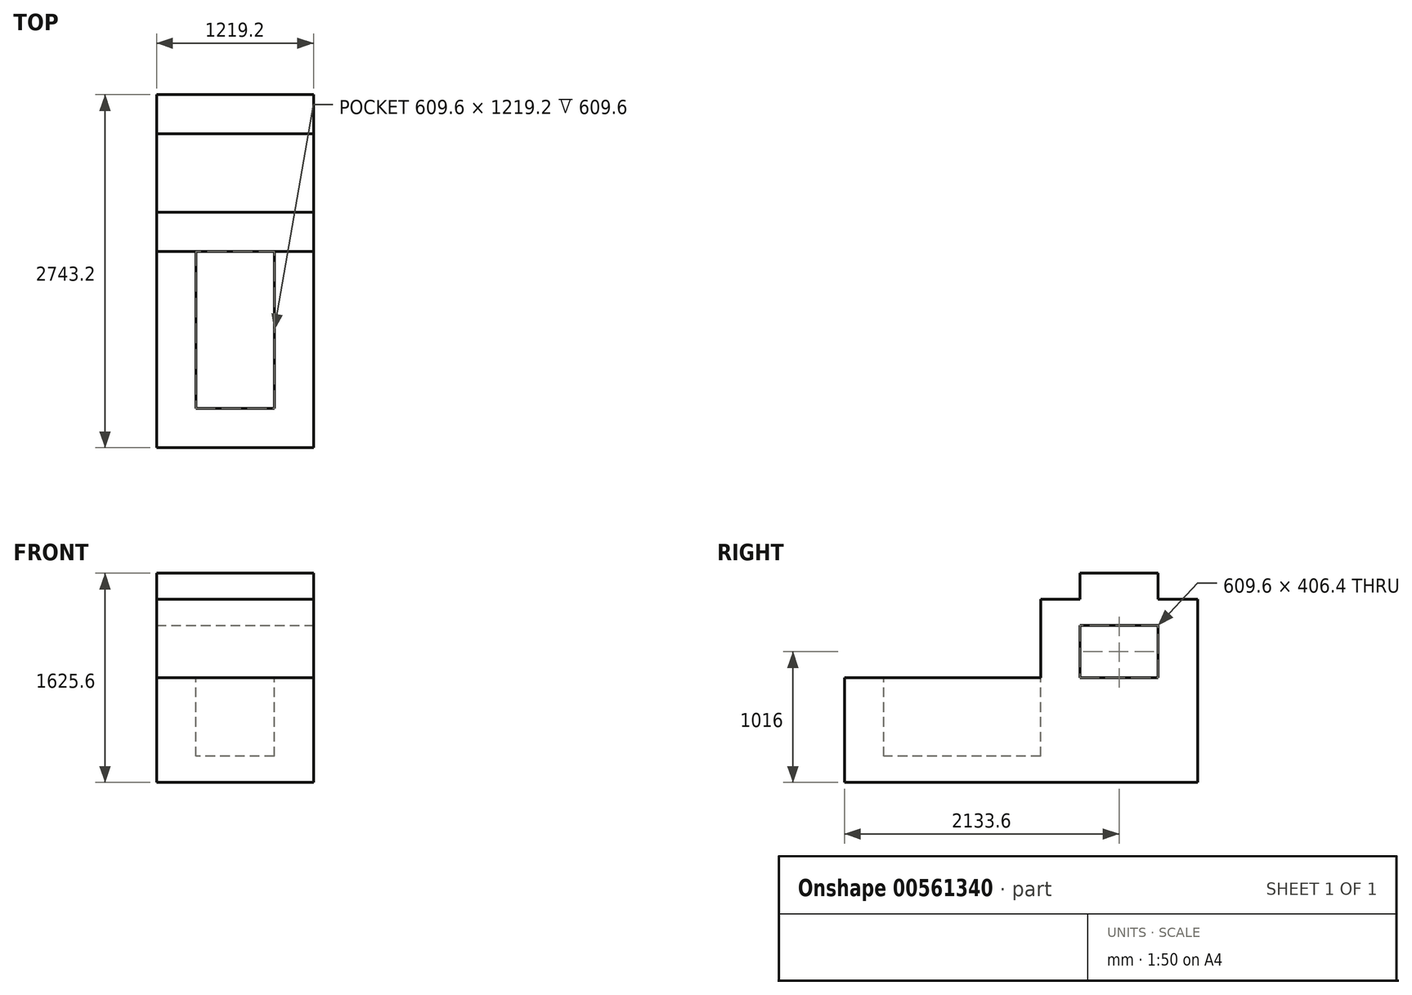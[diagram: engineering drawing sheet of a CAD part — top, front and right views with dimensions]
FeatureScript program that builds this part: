
annotation { "Feature Type Name" : "Feature", "Feature Type Description" : "" }
export const myFeature = defineFeature(function(context is Context, id is Id, definition is map)
    precondition{}
    {
        {
            var Q0;
            Q0=qCreatedBy(makeId("Right.planeOp"),FACE);
            var sketch = newSketch(context, id + "F0", { "sketchPlane" : qUnion([Q0])});
            skLineSegment(sketch, "E0.bottom", {"start": v(-1367.21, -435.68) * mm, "end": v(1375.99, -435.68) * mm});
            skLineSegment(sketch, "E0.left", {"start": v(-1367.21, -435.68) * mm, "end": v(-1367.21, 377.12) * mm});
            skLineSegment(sketch, "E1.top", {"start": v(1375.99, 1189.92) * mm, "end": v(156.79, 1189.92) * mm});
            skLineSegment(sketch, "E1.right", {"start": v(156.79, 377.12) * mm, "end": v(156.79, 1189.92) * mm});
            skLineSegment(sketch, "E2", {"start": v(-1367.21, 377.12) * mm, "end": v(156.79, 377.12) * mm});
            skLineSegment(sketch, "E3", {"start": v(1375.99, 1189.92) * mm, "end": v(1375.99, -435.68) * mm});
            skSolve(sketch);
        }
        {
            var Q0;
            Q0 = qSketchRegion(id + "F0", true);
            extrude(context, id + "F1", {"entities" : qUnion([Q0]), "depth" : 1219.2 * mm, "offsetDistance" : 25.4 * mm});
        }
        {
            var Q0;
            Q0=makeQuery(id+"F1.opExtrude","SWEPT_FACE",FACE,{"disambiguationData":[OSD([sQuery(id+"F0.wireOp",EDGE,"E1.top")])]});
            var sketch = newSketch(context, id + "F2", { "sketchPlane" : qUnion([Q0])});
            skLineSegment(sketch, "E4.bottom", {"start": v(0, 1375.99) * mm, "end": v(1219.2, 1375.99) * mm});
            skLineSegment(sketch, "E4.top", {"start": v(0, 1071.19) * mm, "end": v(1219.2, 1071.19) * mm});
            skLineSegment(sketch, "E4.left", {"start": v(0, 1375.99) * mm, "end": v(0, 1071.19) * mm});
            skLineSegment(sketch, "E4.right", {"start": v(1219.2, 1375.99) * mm, "end": v(1219.2, 1071.19) * mm});
            skLineSegment(sketch, "E5.top", {"start": v(0, 461.59) * mm, "end": v(1219.2, 461.59) * mm});
            skLineSegment(sketch, "E5.left", {"start": v(0, 1071.19) * mm, "end": v(0, 461.59) * mm});
            skLineSegment(sketch, "E5.right", {"start": v(1219.2, 1071.19) * mm, "end": v(1219.2, 461.59) * mm});
            skSolve(sketch);
        }
        {
            var Q0;
            Q0=makeQuery(id+"F2.imprint","IMPRINT",FACE,{"disambiguationData":[TD([[makeQuery(id+"F2.imprint","IMPRINT",EDGE,{"derivedFrom":sQuery(id+"F2.wireOp",EDGE,"E4.bottom")}),1.0]])]});
            extrude(context, id + "F3", {"entities" : qUnion([Q0]), "operationType" : NewBodyOperationType.REMOVE, "oppositeDirection" : true, "depth" : 203.2 * mm, "offsetDistance" : 25.4 * mm});
        }
        {
            var Q0;
            {var subQ0=sQuery(id+"F2.wireOp",EDGE,"E5.top");Q0=makeQuery(id+"F2.imprint","IMPRINT",FACE,{"disambiguationData":[TD([[makeQuery(id+"F2.imprint","IMPRINT",EDGE,{"derivedFrom":subQ0}),-1.0]])]});}
            extrude(context, id + "F4", {"entities" : qUnion([Q0]), "operationType" : NewBodyOperationType.REMOVE, "oppositeDirection" : true, "depth" : 203.2 * mm, "offsetDistance" : 25.4 * mm});
        }
        {
            var Q0;
            Q0=makeQuery(id+"F1.opExtrude","CAP_FACE",FACE,{"disambiguationData":[OSD([sQuery(id+"F0.wireOp",EDGE,"E0.bottom"),sQuery(id+"F0.wireOp",EDGE,"E0.left"),sQuery(id+"F0.wireOp",EDGE,"E1.top"),sQuery(id+"F0.wireOp",EDGE,"E1.right"),sQuery(id+"F0.wireOp",EDGE,"E2"),sQuery(id+"F0.wireOp",EDGE,"E3")])],"isStart":false});
            var sketch = newSketch(context, id + "F5", { "sketchPlane" : qUnion([Q0])});
            skLineSegment(sketch, "E6.top", {"start": v(1071.19, 377.12) * mm, "end": v(461.59, 377.12) * mm});
            skLineSegment(sketch, "E7", {"start": v(1071.19, 377.12) * mm, "end": v(1071.19, 783.52) * mm});
            skLineSegment(sketch, "E8", {"start": v(1071.19, 783.52) * mm, "end": v(461.59, 783.52) * mm});
            skLineSegment(sketch, "E9", {"start": v(461.59, 783.52) * mm, "end": v(461.59, 377.12) * mm});
            skSolve(sketch);
        }
        {
            var Q0;
            Q0=makeQuery(id+"F1.opExtrude","SWEPT_FACE",FACE,{"disambiguationData":[OSD([sQuery(id+"F0.wireOp",EDGE,"E2")])]});
            var sketch = newSketch(context, id + "F6", { "sketchPlane" : qUnion([Q0])});
            skLineSegment(sketch, "E10", {"start": v(0, 156.79) * mm, "end": v(304.8, 156.79) * mm});
            skLineSegment(sketch, "E11.bottom", {"start": v(304.8, 156.79) * mm, "end": v(914.4, 156.79) * mm});
            skLineSegment(sketch, "E11.top", {"start": v(304.8, -1062.41) * mm, "end": v(914.4, -1062.41) * mm});
            skLineSegment(sketch, "E11.left", {"start": v(304.8, 156.79) * mm, "end": v(304.8, -1062.41) * mm});
            skLineSegment(sketch, "E11.right", {"start": v(914.4, 156.79) * mm, "end": v(914.4, -1062.41) * mm});
            skSolve(sketch);
        }
        {
            var Q0;
            Q0=makeQuery(id+"F6.imprint","IMPRINT",FACE,{"disambiguationData":[TD([[makeQuery(id+"F6.imprint","IMPRINT",EDGE,{"derivedFrom":sQuery(id+"F6.wireOp",EDGE,"E11.bottom")}),1.0]])]});
            extrude(context, id + "F7", {"entities" : qUnion([Q0]), "operationType" : NewBodyOperationType.REMOVE, "oppositeDirection" : true, "depth" : 609.6 * mm, "offsetDistance" : 25.4 * mm});
        }
        {
            var Q0;
            Q0=makeQuery(id+"F5.imprint","IMPRINT",FACE,{"disambiguationData":[TD([[makeQuery(id+"F5.imprint","IMPRINT",EDGE,{"derivedFrom":sQuery(id+"F5.wireOp",EDGE,"E6.top")}),-1.0]])]});
            extrude(context, id + "F8", {"entities" : qUnion([Q0]), "operationType" : NewBodyOperationType.REMOVE, "endBound" : BoundingType.THROUGH_ALL, "oppositeDirection" : true, "depth" : 25.4 * mm, "offsetDistance" : 25.4 * mm});
        }
    });
